# Revit family: ПК-ВО
name_source: partatom
category: Арматура воздуховодов
units: mm (PartAtom-declared; Revit-internal decimal feet)

## family parameters
Всегда вертикально = Да
На основе рабочей плоскости = Нет
Общий = Нет
При загрузке вырезать с полостями = Нет
Размер круглого соединителя = Использовать диаметр
Тип детали = Присоединяется

## types (11) — shared parameters
00_20_Manufacturer = Вентс
00_20_Name = Даховий перехідник
Casing Material = Условный материал-отделка
Grid Material = Условный материал-отделка
Load Classification = HVAC
Maintenance zone material = <По категории>
zero-valued in all types: Отметка по умолчанию

## per-type parameters (varying)
| type | A | B | D2 | Dn | Dy | H | K | h | k | Вес |
| ПК-ВО-400 | 580 мм | 701 мм | 490 мм | 410 мм | 400 мм | 170 мм | 217 мм | 20 мм | 205 мм | 17.5 кг |
| ПК-ВО-450 | 580 мм | 701 мм | 540 мм | 460 мм | 450 мм | 170 мм | 197 мм | 20 мм | 230 мм | 16.5 кг |
| ПК-ВО-1250 | 1500 мм | 1700 мм | 1400 мм | 1260 мм | 1250 мм | 340 мм | 376 мм | 40 мм | 630 мм | 107 кг |
| ПК-ВО-1120 | 1340 мм | 1510 мм | 1270 мм | 1130 мм | 1120 мм | 340 мм | 333 мм | 40 мм | 565 мм | 91.3 кг |
| ПК-ВО-500 | 640 мм | 770 мм | 600 мм | 510 мм | 500 мм | 170 мм | 211 мм | 20 мм | 255 мм | 20.3 кг |
| ПК-ВО-560 | 750 мм | 920 мм | 660 мм | 570 мм | 560 мм | 170 мм | 262 мм | 20 мм | 285 мм | 27.2 кг |
| ПК-ВО-630 | 750 мм | 920 мм | 730 мм | 640 мм | 630 мм | 170 мм | 234 мм | 20 мм | 320 мм | 25.5 кг |
| ПК-ВО-710 | 980 мм | 1150 мм | 810 мм | 720 мм | 710 мм | 290 мм | 317 мм | 40 мм | 360 мм | 53 кг |
| ПК-ВО-800 | 980 мм | 1150 мм | 900 мм | 810 мм | 800 мм | 290 мм | 281 мм | 40 мм | 405 мм | 51.1 кг |
| ПК-ВО-900 | 1050 мм | 1220 мм | 1015 мм | 910 мм | 900 мм | 290 мм | 276 мм | 40 мм | 455 мм | 54.5 кг |
| ПК-ВО-1000 | 1340 мм | 1510 мм | 1115 мм | 1010 мм | 1000 мм | 340 мм | 381 мм | 40 мм | 505 мм | 93.4 кг |

note: column(s) folded — value = type name in every type: 00_20_Type
